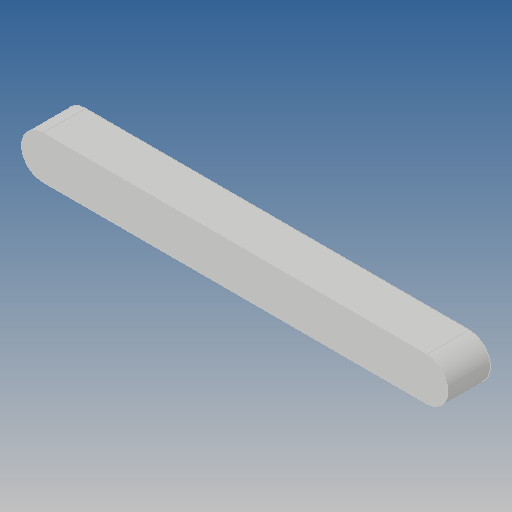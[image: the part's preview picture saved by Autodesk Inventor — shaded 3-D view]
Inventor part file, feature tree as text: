
AUTODESK INVENTOR PART (.ipt)
format: ipt  version: 2018 (Build 220112000, 112)  size: 86,528 bytes
history: native  units: mm
features: extrude x1
ambient origin geometry x8: Origin, YZ Plane, XZ Plane, XY Plane, X Axis, Y Axis, Z Axis, Center Point
bodies: Solid1 (feature_tree)
feature tree (1):
  extrude  "Extrude2"  [1 undecoded]
note: 1 required parameter value undecoded (feature->parameter linkage not recoverable at this tier; creation-order binding heuristic only, values carry confidence <= 0.55)
